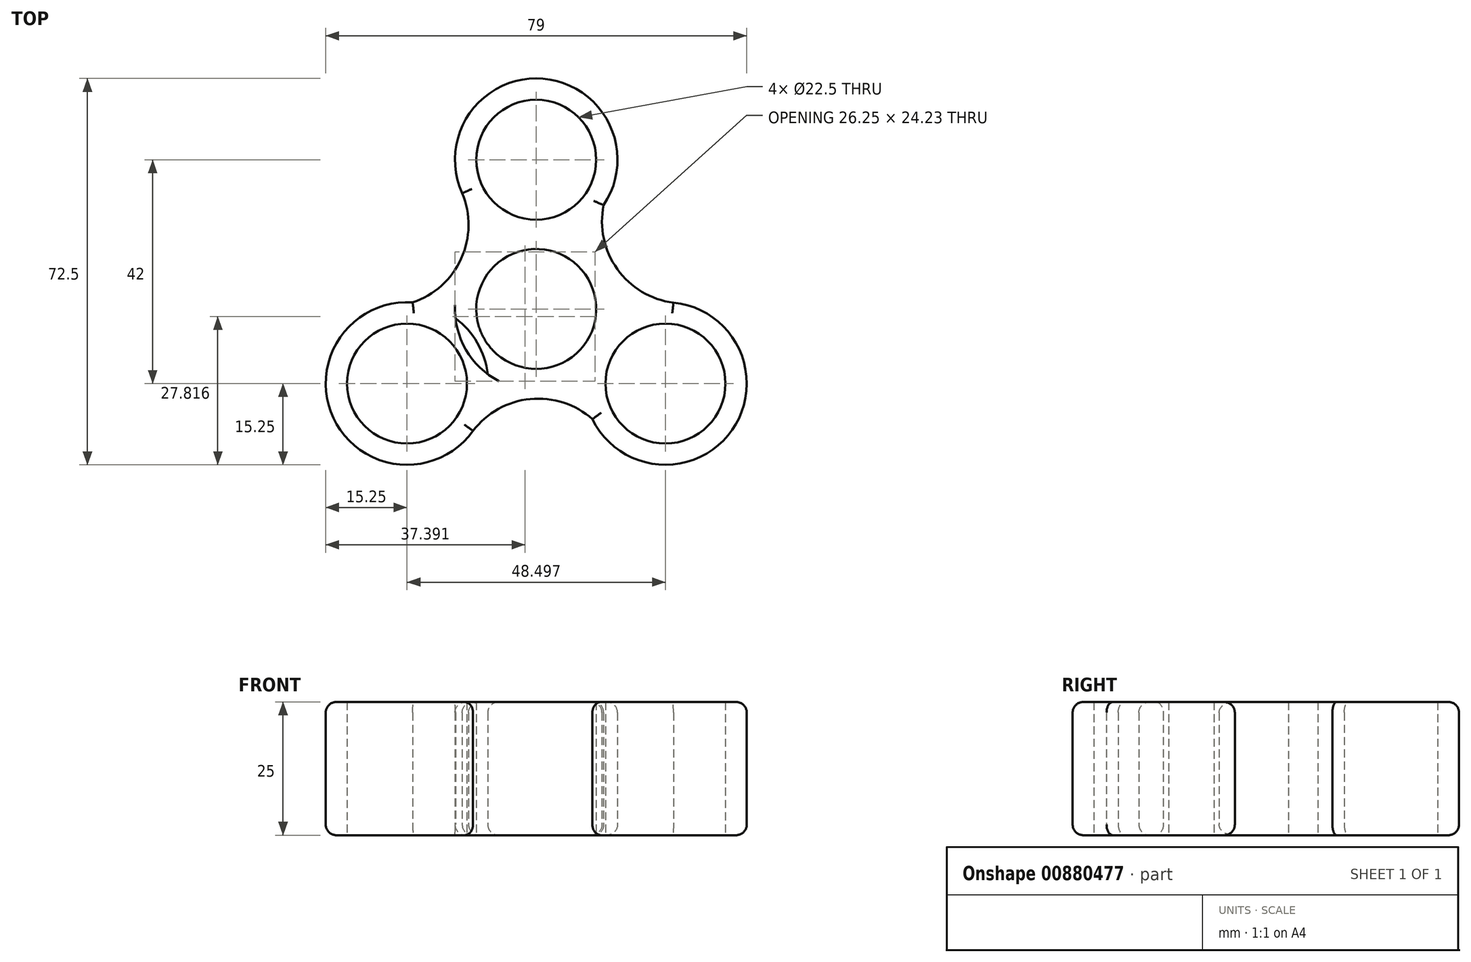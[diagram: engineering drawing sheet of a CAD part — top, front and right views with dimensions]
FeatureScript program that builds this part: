
annotation { "Feature Type Name" : "Feature", "Feature Type Description" : "" }
export const myFeature = defineFeature(function(context is Context, id is Id, definition is map)
    precondition{}
    {
        {
            var Q0;
            Q0=qCreatedBy(makeId("Top.planeOp"),FACE);
            var sketch = newSketch(context, id + "F0", { "sketchPlane" : qUnion([Q0])});
            skCircle(sketch, "E0", {"center": v(-115.03, 105.54) * mm, "radius": 11.25 * mm});
            skCircle(sketch, "E1", {"center": v(-115.03, 133.54) * mm, "radius": 11.25 * mm});
            skCircle(sketch, "E2.1.0", {"center": v(-139.28, 91.54) * mm, "radius": 11.25 * mm});
            skCircle(sketch, "E2.2.0", {"center": v(-90.78, 91.54) * mm, "radius": 11.25 * mm});
            skCircle(sketch, "E3.0", {"center": v(-115.03, 133.54) * mm, "radius": 15.25 * mm});
            skCircle(sketch, "E4.0", {"center": v(-139.28, 91.54) * mm, "radius": 15.25 * mm});
            skCircle(sketch, "E5.0", {"center": v(-115.03, 105.54) * mm, "radius": 15.25 * mm});
            skCircle(sketch, "E6.0", {"center": v(-90.78, 91.54) * mm, "radius": 15.25 * mm});
            skArc(sketch, "E7", {"start": v(-138.23, 106.75) * mm, "mid": v(-129.1, 114.98) * mm, "end": v(-128.93, 127.26) * mm});
            skArc(sketch, "E8.1.0", {"start": v(-104.49, 84.85) * mm, "mid": v(-116.17, 88.63) * mm, "end": v(-126.9, 82.65) * mm});
            skArc(sketch, "E8.2.0", {"start": v(-102.38, 125.02) * mm, "mid": v(-99.82, 113) * mm, "end": v(-89.27, 106.71) * mm});
            skSolve(sketch);
        }
        {
            var Q0;
            Q0=makeQuery(id+"F0.imprint","IMPRINT",FACE,{"disambiguationData":[TD([[makeQuery(id+"F0.imprint","IMPRINT",EDGE,{"derivedFrom":sQuery(id+"F0.wireOp",EDGE,"E1")}),-1.0]])]});
            var Q1;
            Q1=makeQuery(id+"F0.imprint","IMPRINT",FACE,{"disambiguationData":[TD([[makeQuery(id+"F0.imprint","IMPRINT",EDGE,{"derivedFrom":sQuery(id+"F0.wireOp",EDGE,"E2.2.0")}),-1.0]])]});
            var Q2;
            Q2=makeQuery(id+"F0.imprint","IMPRINT",FACE,{"disambiguationData":[TD([[makeQuery(id+"F0.imprint","IMPRINT",EDGE,{"derivedFrom":sQuery(id+"F0.wireOp",EDGE,"E0")}),-1.0]])]});
            var Q3;
            Q3=makeQuery(id+"F0.imprint","IMPRINT",FACE,{"disambiguationData":[TD([[makeQuery(id+"F0.imprint","IMPRINT",EDGE,{"derivedFrom":sQuery(id+"F0.wireOp",EDGE,"E2.1.0")}),-1.0]])]});
            var Q4;
            {var subQ0=sQuery(id+"F0.wireOp",EDGE,"E5.0");var subQ1=sQuery(id+"F0.wireOp",EDGE,"E4.0");var subQ2=makeQuery(id+"F0.imprint","INTERSECT",VERTEX,{"disambiguationData":[OD(0.0)],"derivedFrom":[subQ1,subQ0]});Q4=makeQuery(id+"F0.imprint","IMPRINT",FACE,{"disambiguationData":[TD([[makeQuery(id+"F0.imprint","IMPRINT",EDGE,{"disambiguationData":[TD([[subQ2,-1.0]])],"derivedFrom":subQ1}),1.0]])]});}
            var Q5;
            {var subQ0=sQuery(id+"F0.wireOp",EDGE,"E6.0");var subQ1=sQuery(id+"F0.wireOp",EDGE,"E5.0");var subQ2=makeQuery(id+"F0.imprint","INTERSECT",VERTEX,{"disambiguationData":[OD(0.0)],"derivedFrom":[subQ1,subQ0]});Q5=makeQuery(id+"F0.imprint","IMPRINT",FACE,{"disambiguationData":[TD([[makeQuery(id+"F0.imprint","IMPRINT",EDGE,{"disambiguationData":[TD([[subQ2,-1.0]])],"derivedFrom":subQ1}),1.0]])]});}
            var Q6;
            {var subQ0=sQuery(id+"F0.wireOp",EDGE,"E5.0");var subQ1=sQuery(id+"F0.wireOp",EDGE,"E3.0");var subQ2=makeQuery(id+"F0.imprint","INTERSECT",VERTEX,{"disambiguationData":[OD(0.0)],"derivedFrom":[subQ1,subQ0]});Q6=makeQuery(id+"F0.imprint","IMPRINT",FACE,{"disambiguationData":[TD([[makeQuery(id+"F0.imprint","IMPRINT",EDGE,{"disambiguationData":[TD([[subQ2,-1.0]])],"derivedFrom":subQ1}),1.0]])]});}
            var Q7;
            {var subQ0=sQuery(id+"F0.wireOp",EDGE,"E7");Q7=makeQuery(id+"F0.imprint","IMPRINT",FACE,{"disambiguationData":[TD([[makeQuery(id+"F0.imprint","IMPRINT",EDGE,{"derivedFrom":subQ0}),-1.0]])]});}
            var Q8;
            {var subQ0=sQuery(id+"F0.wireOp",EDGE,"E8.2.0");Q8=makeQuery(id+"F0.imprint","IMPRINT",FACE,{"disambiguationData":[TD([[makeQuery(id+"F0.imprint","IMPRINT",EDGE,{"derivedFrom":subQ0}),-1.0]])]});}
            var Q9;
            {var subQ0=sQuery(id+"F0.wireOp",EDGE,"E8.1.0");Q9=makeQuery(id+"F0.imprint","IMPRINT",FACE,{"disambiguationData":[TD([[makeQuery(id+"F0.imprint","IMPRINT",EDGE,{"derivedFrom":subQ0}),-1.0]])]});}
            extrude(context, id + "F1", {"entities" : qUnion([Q0, Q1, Q2, Q3, Q4, Q5, Q6, Q7, Q8, Q9]), "depth" : 25 * mm, "offsetDistance" : 25 * mm});
        }
        {
            var Q0;
            Q0=makeQuery(id+"F1.opExtrude","CAP_EDGE",EDGE,{"disambiguationData":[OSD([sQuery(id+"F0.wireOp",EDGE,"E8.2.0")])],"isStart":false});
            var Q1;
            Q1=makeQuery(id+"F1.opExtrude","CAP_EDGE",EDGE,{"disambiguationData":[OSD([sQuery(id+"F0.wireOp",EDGE,"E3.0")])],"isStart":false});
            var Q2;
            Q2=makeQuery(id+"F1.opExtrude","CAP_EDGE",EDGE,{"disambiguationData":[OSD([sQuery(id+"F0.wireOp",EDGE,"E4.0")])],"isStart":false});
            var Q3;
            Q3=makeQuery(id+"F1.opExtrude","CAP_EDGE",EDGE,{"disambiguationData":[OSD([sQuery(id+"F0.wireOp",EDGE,"E6.0")])],"isStart":false});
            var Q4;
            Q4=makeQuery(id+"F1.opExtrude","CAP_EDGE",EDGE,{"disambiguationData":[OSD([sQuery(id+"F0.wireOp",EDGE,"E7")])],"isStart":true});
            var Q5;
            Q5=makeQuery(id+"F1.opExtrude","CAP_EDGE",EDGE,{"disambiguationData":[OSD([sQuery(id+"F0.wireOp",EDGE,"E4.0")])],"isStart":true});
            var Q6;
            Q6=makeQuery(id+"F1.opExtrude","CAP_EDGE",EDGE,{"disambiguationData":[OSD([sQuery(id+"F0.wireOp",EDGE,"E6.0")])],"isStart":true});
            var Q7;
            Q7=makeQuery(id+"F1.opExtrude","CAP_EDGE",EDGE,{"disambiguationData":[OSD([sQuery(id+"F0.wireOp",EDGE,"E3.0")])],"isStart":true});
            fillet(context, id + "F2", {"entities" : qUnion([Q0, Q1, Q2, Q3, Q4, Q5, Q6, Q7]), "radius" : 2 * mm, "tangentPropagation" : true, "allowEdgeOverflow" : false});
        }
    });
